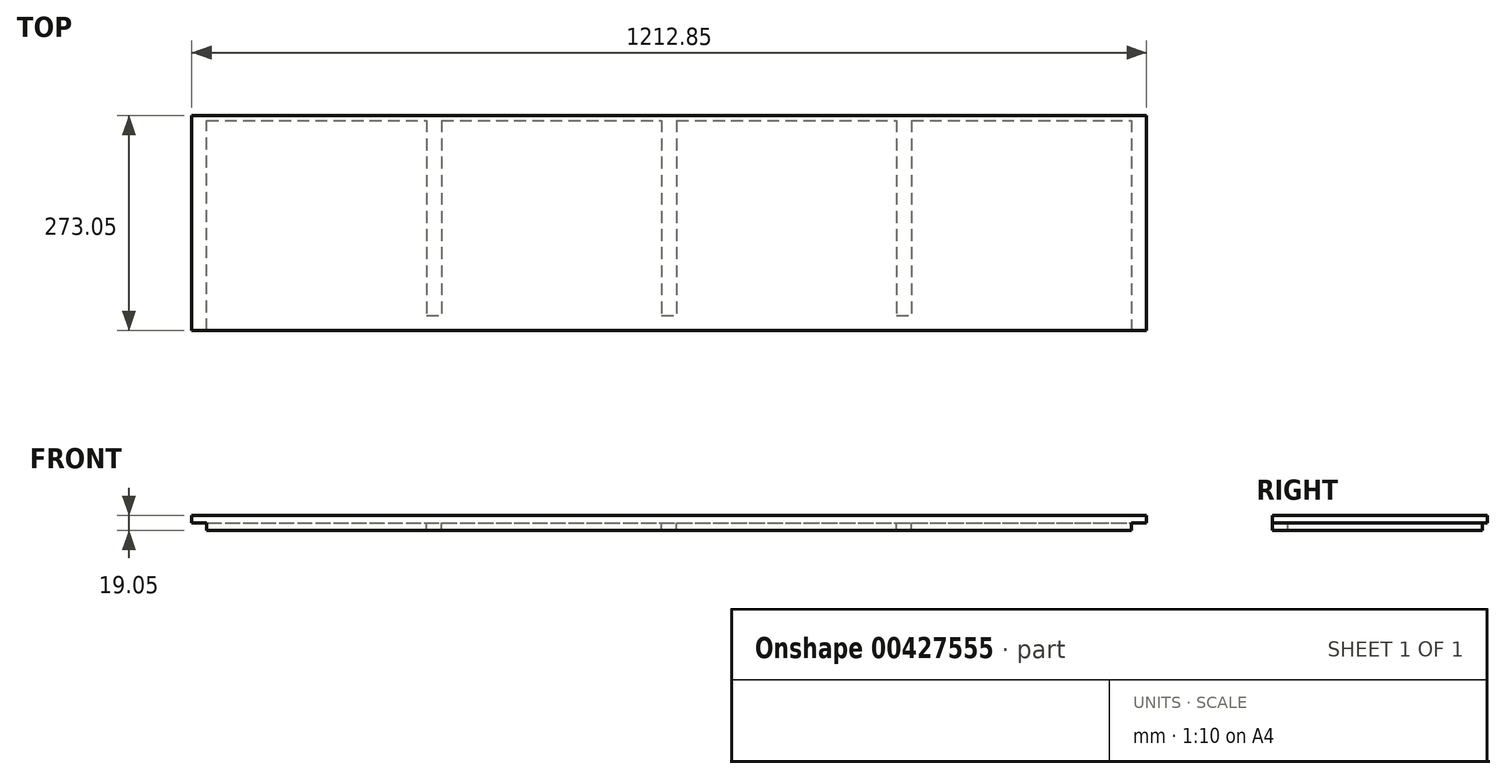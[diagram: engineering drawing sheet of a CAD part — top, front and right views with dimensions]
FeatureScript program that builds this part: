
annotation { "Feature Type Name" : "Feature", "Feature Type Description" : "" }
export const myFeature = defineFeature(function(context is Context, id is Id, definition is map)
    precondition{}
    {
        {
            var Q0;
            Q0=qCreatedBy(makeId("Top.planeOp"),FACE);
            var sketch = newSketch(context, id + "F0", { "sketchPlane" : qUnion([Q0])});
            skLineSegment(sketch, "E0.bottom", {"start": v(0, 0) * mm, "end": v(1212.85, 0) * mm});
            skLineSegment(sketch, "E0.top", {"start": v(0, 273.05) * mm, "end": v(1212.85, 273.05) * mm});
            skLineSegment(sketch, "E0.left", {"start": v(0, 0) * mm, "end": v(0, 273.05) * mm});
            skLineSegment(sketch, "E0.right", {"start": v(1212.85, 0) * mm, "end": v(1212.85, 273.05) * mm});
            skSolve(sketch);
        }
        {
            var Q0;
            Q0 = qSketchRegion(id + "F0", true);
            extrude(context, id + "F1", {"entities" : qUnion([Q0]), "depth" : 19.05 * mm});
        }
        {
            var Q0;
            Q0=makeQuery(id+"F1.opExtrude","CAP_FACE",FACE,{"disambiguationData":[OSD([sQuery(id+"F0.wireOp",EDGE,"E0.bottom"),sQuery(id+"F0.wireOp",EDGE,"E0.top"),sQuery(id+"F0.wireOp",EDGE,"E0.left"),sQuery(id+"F0.wireOp",EDGE,"E0.right")])],"isStart":true});
            var sketch = newSketch(context, id + "F2", { "sketchPlane" : qUnion([Q0])});
            skLineSegment(sketch, "E1.bottom", {"start": v(0, 0) * mm, "end": v(19.05, 0) * mm});
            skLineSegment(sketch, "E1.top", {"start": v(0, -273.05) * mm, "end": v(19.05, -273.05) * mm});
            skLineSegment(sketch, "E1.left", {"start": v(0, 0) * mm, "end": v(0, -273.05) * mm});
            skLineSegment(sketch, "E1.right", {"start": v(19.05, 0) * mm, "end": v(19.05, -273.05) * mm});
            skLineSegment(sketch, "E2.bottom", {"start": v(298.45, -273.05) * mm, "end": v(317.5, -273.05) * mm});
            skLineSegment(sketch, "E2.top", {"start": v(298.45, -19.05) * mm, "end": v(317.5, -19.05) * mm});
            skLineSegment(sketch, "E2.left", {"start": v(298.45, -273.05) * mm, "end": v(298.45, -19.05) * mm});
            skLineSegment(sketch, "E2.right", {"start": v(317.5, -273.05) * mm, "end": v(317.5, -19.05) * mm});
            skLineSegment(sketch, "E3.bottom", {"start": v(596.9, -273.05) * mm, "end": v(615.95, -273.05) * mm});
            skLineSegment(sketch, "E3.top", {"start": v(596.9, -19.05) * mm, "end": v(615.95, -19.05) * mm});
            skLineSegment(sketch, "E3.left", {"start": v(596.9, -273.05) * mm, "end": v(596.9, -19.05) * mm});
            skLineSegment(sketch, "E3.right", {"start": v(615.95, -273.05) * mm, "end": v(615.95, -19.05) * mm});
            skLineSegment(sketch, "E4.bottom", {"start": v(895.35, -273.05) * mm, "end": v(914.4, -273.05) * mm});
            skLineSegment(sketch, "E4.top", {"start": v(895.35, -19.05) * mm, "end": v(914.4, -19.05) * mm});
            skLineSegment(sketch, "E4.left", {"start": v(895.35, -273.05) * mm, "end": v(895.35, -19.05) * mm});
            skLineSegment(sketch, "E4.right", {"start": v(914.4, -273.05) * mm, "end": v(914.4, -19.05) * mm});
            skLineSegment(sketch, "E5.bottom", {"start": v(1212.85, -273.05) * mm, "end": v(1193.8, -273.05) * mm});
            skLineSegment(sketch, "E5.top", {"start": v(1212.85, 0) * mm, "end": v(1193.8, 0) * mm});
            skLineSegment(sketch, "E5.left", {"start": v(1212.85, -273.05) * mm, "end": v(1212.85, 0) * mm});
            skLineSegment(sketch, "E5.right", {"start": v(1193.8, -273.05) * mm, "end": v(1193.8, 0) * mm});
            skSolve(sketch);
        }
        {
            var Q0;
            Q0 = qSketchRegion(id + "F2", true);
            extrude(context, id + "F3", {"entities" : qUnion([Q0]), "operationType" : NewBodyOperationType.REMOVE, "oppositeDirection" : true, "depth" : 9.52 * mm});
        }
        {
            var Q0;
            Q0=makeQuery(id+"F1.opExtrude","CAP_FACE",FACE,{"disambiguationData":[OSD([sQuery(id+"F0.wireOp",EDGE,"E0.bottom"),sQuery(id+"F0.wireOp",EDGE,"E0.top"),sQuery(id+"F0.wireOp",EDGE,"E0.left"),sQuery(id+"F0.wireOp",EDGE,"E0.right")])],"isStart":true});
            var sketch = newSketch(context, id + "F4", { "sketchPlane" : qUnion([Q0])});
            skLineSegment(sketch, "E6.bottom", {"start": v(19.05, -273.05) * mm, "end": v(1193.8, -273.05) * mm});
            skLineSegment(sketch, "E6.top", {"start": v(19.05, -266.7) * mm, "end": v(1193.8, -266.7) * mm});
            skLineSegment(sketch, "E6.left", {"start": v(19.05, -273.05) * mm, "end": v(19.05, -266.7) * mm});
            skLineSegment(sketch, "E6.right", {"start": v(1193.8, -273.05) * mm, "end": v(1193.8, -266.7) * mm});
            skSolve(sketch);
        }
        {
            var Q0;
            Q0 = qSketchRegion(id + "F4", true);
            extrude(context, id + "F5", {"entities" : qUnion([Q0]), "operationType" : NewBodyOperationType.REMOVE, "oppositeDirection" : true, "depth" : 9.52 * mm});
        }
    });
